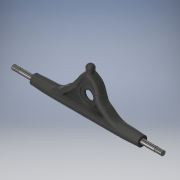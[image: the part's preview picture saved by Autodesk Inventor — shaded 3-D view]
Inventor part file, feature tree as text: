
AUTODESK INVENTOR PART (.ipt)
format: ipt  version: 2019.4 (Build 234330000, 330)  size: 7,098,880 bytes
history: native  units: mm
features: sketch x12, extrude x12, fillet x10, other x4, chamfer x3, plane x3, thread x2, revolve x1, thicken_offset x1, surface_op x1
ambient origin geometry x8: Origin, YZ Plane, XZ Plane, XY Plane, X Axis, Y Axis, Z Axis, Center Point
bodies: Solid1 (feature_tree)
feature tree (49):
  revolve  "Revolution1"  [1 undecoded]
  sketch  "Sketch2"  dims[d20=9.5mm d21=8.0mm d29=9.4mm]
  sketch  "Sketch3"  dims[d32=8.4mm d33=9.0mm d34=9.5mm d35=9.5mm]
  thicken_offset  "Thicken2"
  extrude  "Extrusion2"  Depth=8.0mm
  fillet  "Fillet1"  Radius=9.4mm
  extrude  "Extrusion3"  Depth=9.0mm
  fillet  "Fillet2"  Radius=9.5mm
  fillet  "Fillet3"  Radius=9.5mm
  extrude  "Extrusion4"  Depth=15.0mm
  fillet  "Fillet4"  Radius=25.0mm
  extrude  "Extrusion5"  Depth=15.0mm
  fillet  "Fillet5"  Radius=65.0mm
  extrude  "Extrusion6"  TaperAngle=90.0deg  [1 undecoded]
  fillet  "Fillet6"  [1 undecoded]
  fillet  "Fillet7"  Radius=18.0mm
  chamfer  "Chamfer1"  Distance=10.0mm
  extrude  "Extrusion8"  Depth=59.0mm
  fillet  "Fillet10"  Radius=10.0mm
  fillet  "Fillet11"  Radius=0.5mm
  extrude  "Extrusion9"  Depth=4.0mm TaperAngle=0.0deg
  extrude  "Extrusion10"  Depth=6.0mm TaperAngle=0.0deg
  chamfer  "Chamfer2"  Distance=6.0mm
  extrude  "Extrusion11"  Depth=0.5mm
  extrude  "Extrusion12"  Depth=0.5mm
  chamfer  "Chamfer3"  Distance=1.0mm Angle=45.0deg
  plane  "Work Plane2"
  sketch  "Sketch12"  dims[d145=1.0mm d146=6.0mm d147=2.0mm d148=0.0mm d149=0.0mm]
  plane  "Work Plane3"
  sketch  "Sketch13"  dims[d150=1.5mm d151=6.0mm d152=0.0mm d153=0.5mm d154=0.5mm d155=1.0mm d156=2.0mm d157=45.0deg d158=7.5mm d159=12.0mm d166=10.0mm d167=5.0mm d168=0.0mm d169=0.0mm d170=1.0mm d171=5.0mm d172=8.0mm d173=35.0mm d174=0.0mm d175=0.1mm d176=12.0mm d177=0.0mm d178=0.5mm d179=2.0mm d180=45.0deg d181=8.0mm d182=35.0mm d183=0.0mm d184=0.1mm d185=12.0mm d186=0.0mm d187=0.5mm d188=2.0mm d189=45.0deg d192=7.0mm d193=7.0mm d194=0.5mm d195=0.0mm d196=0.5mm d197=0.0mm d198=10.0mm d199=0.0mm d200=10.0mm d201=0.0mm d203=30.5mm d204=0.5mm d205=22.455406mm]
  extrude  "Extrusion13"  Depth=7.5mm
  extrude  "Extrusion14"  Depth=12.0mm
  thread  "Thread1"  [1 undecoded]
  thread  "Thread2"  [1 undecoded]
  fillet  "Fillet13"  Radius=5.0mm
  plane  "Work Plane5"
  sketch  "Sketch1"  dims[d1=65.0mm d2=90.5mm]
  other  "Image1"
  other  "Image4"
  sketch  "Sketch4"  dims[d37=90.0deg d38=15.0mm d39=25.0mm]
  sketch  "3D Sketch2"
  other  "3D Intersection2"
  other  "Srf2"
  sketch  "Sketch6"  dims[d40=32.0mm d41=15.0mm d123=65.0mm]
  sketch  "Sketch7"  dims[d124=15.0mm d125=90.0deg d132=0.0mm d133=18.0mm]
  sketch  "Sketch9"  dims[d134=18.0mm d135=10.0mm d136=0.0mm]
  sketch  "Sketch10"  dims[d137=5.0mm d138=59.0mm d139=10.0mm d140=0.0mm d141=0.5mm]
  sketch  "Sketch11"  dims[d142=0.5mm d143=4.0mm d144=0.0mm]
  surface_op  "Boundary Patch2"
note: 5 required parameter values undecoded (feature->parameter linkage not recoverable at this tier; creation-order binding heuristic only, values carry confidence <= 0.55)